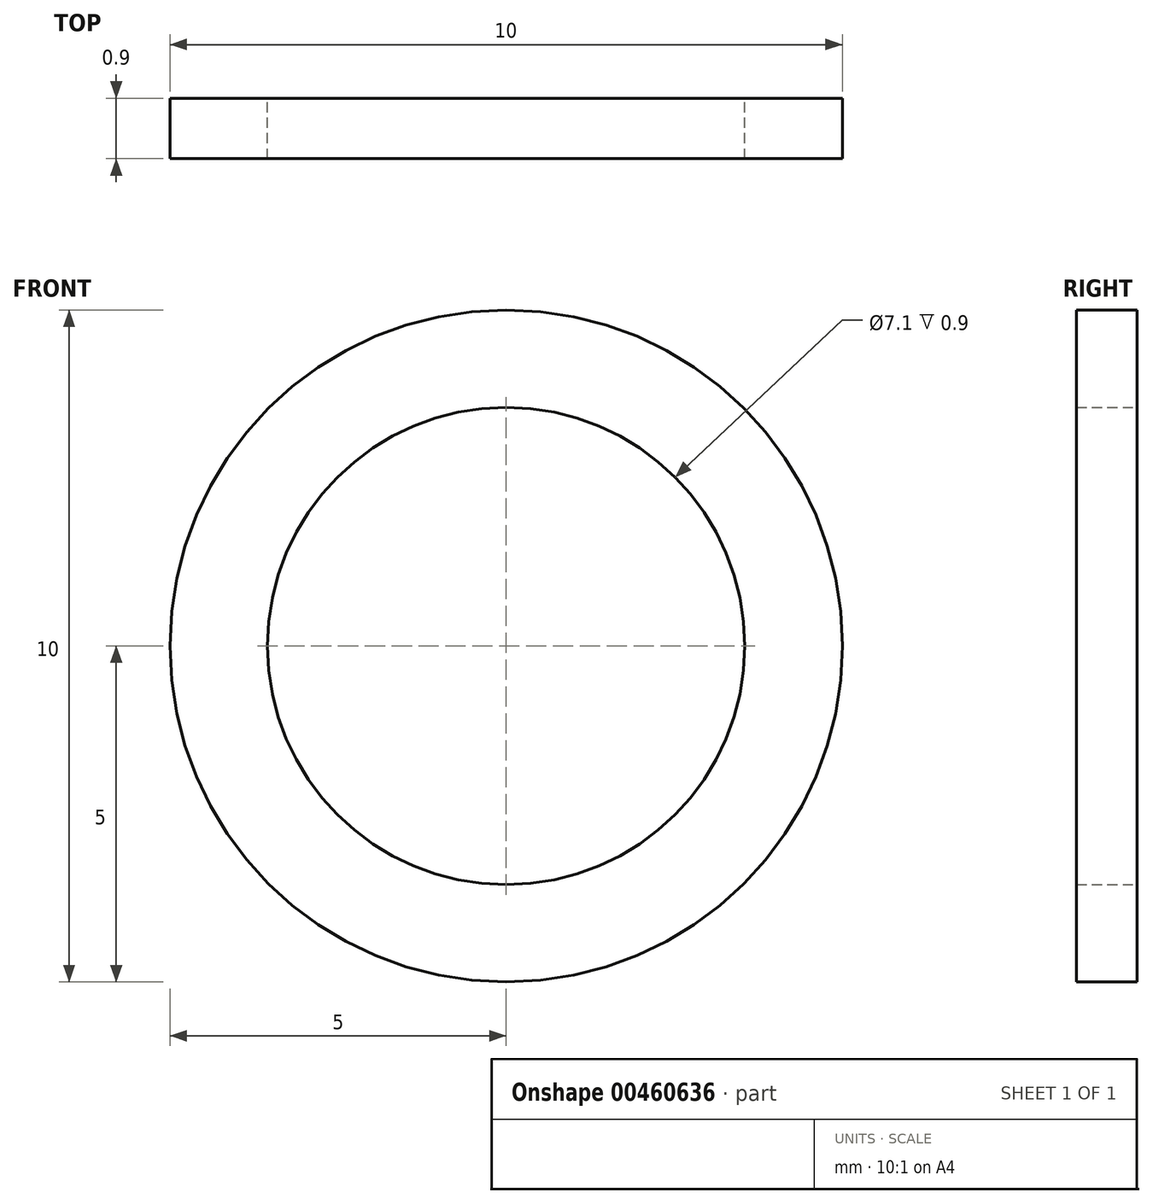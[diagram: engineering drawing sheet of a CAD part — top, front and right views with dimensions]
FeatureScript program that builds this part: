
annotation { "Feature Type Name" : "Feature", "Feature Type Description" : "" }
export const myFeature = defineFeature(function(context is Context, id is Id, definition is map)
    precondition{}
    {
        {
            var Q0;
            Q0=qCreatedBy(makeId("Front.planeOp"),FACE);
            var sketch = newSketch(context, id + "F0", { "sketchPlane" : qUnion([Q0])});
            skCircle(sketch, "E0", {"center": v(0, 0) * mm, "radius": 5 * mm});
            skCircle(sketch, "E1", {"center": v(0, 0) * mm, "radius": 3.55 * mm});
            skSolve(sketch);
        }
        {
            var Q0;
            Q0=makeQuery(id+"F0.imprint","IMPRINT",FACE,{"disambiguationData":[TD([[makeQuery(id+"F0.imprint","IMPRINT",EDGE,{"derivedFrom":sQuery(id+"F0.wireOp",EDGE,"E0")}),1.0]])]});
            extrude(context, id + "F1", {"entities" : qUnion([Q0]), "depth" : 0.9 * mm});
        }
    });
